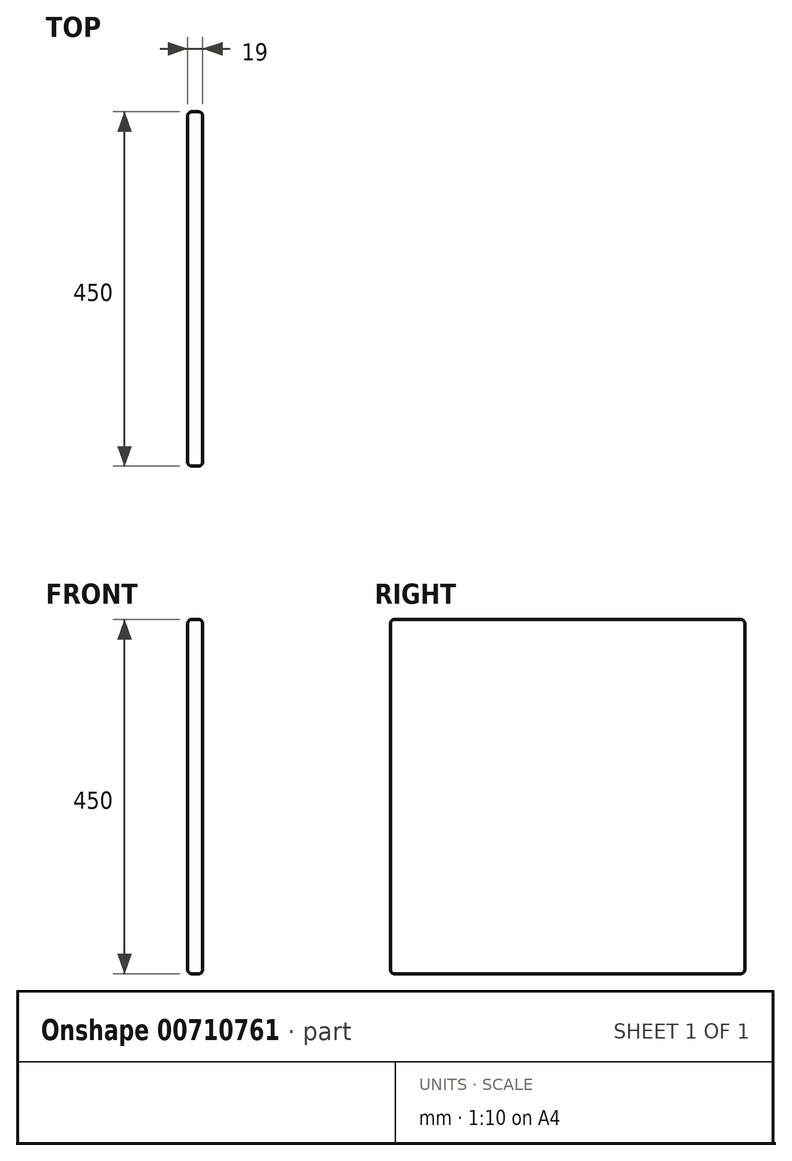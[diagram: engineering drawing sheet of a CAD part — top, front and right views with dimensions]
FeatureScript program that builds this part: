
annotation { "Feature Type Name" : "Feature", "Feature Type Description" : "" }
export const myFeature = defineFeature(function(context is Context, id is Id, definition is map)
    precondition{}
    {
        {
            var Q0;
            Q0=qCreatedBy(makeId("Right.planeOp"),FACE);
            var sketch = newSketch(context, id + "F0", { "sketchPlane" : qUnion([Q0])});
            skLineSegment(sketch, "E0.bottom", {"start": v(-33.4, 467.11) * mm, "end": v(416.6, 467.11) * mm});
            skLineSegment(sketch, "E0.top", {"start": v(-33.4, 17.11) * mm, "end": v(416.6, 17.11) * mm});
            skLineSegment(sketch, "E0.left", {"start": v(-33.4, 467.11) * mm, "end": v(-33.4, 17.11) * mm});
            skLineSegment(sketch, "E0.right", {"start": v(416.6, 467.11) * mm, "end": v(416.6, 17.11) * mm});
            skSolve(sketch);
        }
        {
            var Q0;
            Q0=makeQuery(id+"F0.imprint","IMPRINT",FACE,{"disambiguationData":[TD([[makeQuery(id+"F0.imprint","IMPRINT",EDGE,{"derivedFrom":sQuery(id+"F0.wireOp",EDGE,"E0.bottom")}),-1.0]])]});
            extrude(context, id + "F1", {"entities" : qUnion([Q0]), "depth" : 19 * mm, "offsetDistance" : 25.4 * mm});
        }
        {
            var Q0;
            Q0=makeQuery(id+"F1.opExtrude","SWEPT_EDGE",EDGE,{"disambiguationData":[OSD([sQuery(id+"F0.wireOp",EDGE,"E0.bottom"),sQuery(id+"F0.wireOp",EDGE,"E0.left")])]});
            var Q1;
            Q1=makeQuery(id+"F1.opExtrude","SWEPT_EDGE",EDGE,{"disambiguationData":[OSD([sQuery(id+"F0.wireOp",EDGE,"E0.bottom"),sQuery(id+"F0.wireOp",EDGE,"E0.right")])]});
            var Q2;
            Q2=makeQuery(id+"F1.opExtrude","SWEPT_EDGE",EDGE,{"disambiguationData":[OSD([sQuery(id+"F0.wireOp",EDGE,"E0.top"),sQuery(id+"F0.wireOp",EDGE,"E0.left")])]});
            var Q3;
            Q3=makeQuery(id+"F1.opExtrude","CAP_EDGE",EDGE,{"disambiguationData":[OSD([sQuery(id+"F0.wireOp",EDGE,"E0.bottom")])],"isStart":true});
            var Q4;
            Q4=makeQuery(id+"F1.opExtrude","CAP_EDGE",EDGE,{"disambiguationData":[OSD([sQuery(id+"F0.wireOp",EDGE,"E0.bottom")])],"isStart":false});
            var Q5;
            Q5=makeQuery(id+"F1.opExtrude","CAP_EDGE",EDGE,{"disambiguationData":[OSD([sQuery(id+"F0.wireOp",EDGE,"E0.top")])],"isStart":false});
            var Q6;
            Q6=makeQuery(id+"F1.opExtrude","SWEPT_EDGE",EDGE,{"disambiguationData":[OSD([sQuery(id+"F0.wireOp",EDGE,"E0.top"),sQuery(id+"F0.wireOp",EDGE,"E0.right")])]});
            var Q7;
            Q7=makeQuery(id+"F1.opExtrude","CAP_EDGE",EDGE,{"disambiguationData":[OSD([sQuery(id+"F0.wireOp",EDGE,"E0.top")])],"isStart":true});
            var Q8;
            Q8=makeQuery(id+"F1.opExtrude","CAP_EDGE",EDGE,{"disambiguationData":[OSD([sQuery(id+"F0.wireOp",EDGE,"E0.right")])],"isStart":false});
            var Q9;
            Q9=makeQuery(id+"F1.opExtrude","CAP_EDGE",EDGE,{"disambiguationData":[OSD([sQuery(id+"F0.wireOp",EDGE,"E0.left")])],"isStart":false});
            var Q10;
            Q10=makeQuery(id+"F1.opExtrude","CAP_EDGE",EDGE,{"disambiguationData":[OSD([sQuery(id+"F0.wireOp",EDGE,"E0.right")])],"isStart":true});
            var Q11;
            Q11=makeQuery(id+"F1.opExtrude","CAP_EDGE",EDGE,{"disambiguationData":[OSD([sQuery(id+"F0.wireOp",EDGE,"E0.left")])],"isStart":true});
            fillet(context, id + "F2", {"entities" : qUnion([Q0, Q1, Q2, Q3, Q4, Q5, Q6, Q7, Q8, Q9, Q10, Q11]), "radius" : 5 * mm, "tangentPropagation" : true, "allowEdgeOverflow" : false});
        }
    });
